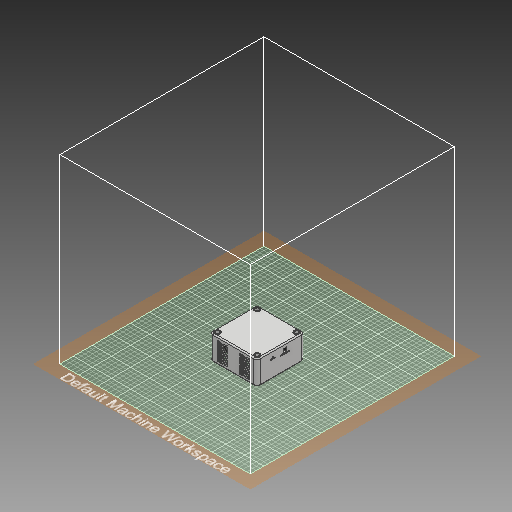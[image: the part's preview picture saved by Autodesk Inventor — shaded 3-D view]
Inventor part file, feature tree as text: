
AUTODESK INVENTOR PART (.ipt)
format: ipt  version: 2019 (Build 230136000, 136)  size: 2,817,024 bytes
history: native  units: mm
features: sketch x17, extrude x15, projected_geometry x15, other x5, fillet x4, reference x2, hole x1
ambient origin geometry x8: Origin, YZ Plane, XZ Plane, XY Plane, X Axis, Y Axis, Z Axis, Center Point
bodies: Body1 (feature_tree)
feature tree (59):
  other  "Твердое тело1"
  extrude  "Выдавливание1"  Depth=0.1mm
  extrude  "Выдавливание2"  Depth=0.3mm
  extrude  "Выдавливание3"  Depth=0.3mm
  fillet  "Сопряжение1"  Radius=0.3mm
  extrude  "Выдавливание5"  Depth=0.3mm
  extrude  "Выдавливание6"  Depth=2.1mm TaperAngle=0.0deg
  extrude  "Выдавливание7"  Depth=49.0mm TaperAngle=0.0deg
  extrude  "Выдавливание8"  Depth=2.5mm TaperAngle=0.0deg
  fillet  "Сопряжение2"  Radius=2.5mm
  fillet  "Сопряжение3"  Radius=12.0mm
  fillet  "Сопряжение4"  Radius=12.0mm
  extrude  "Выдавливание9"  Depth=12.0mm
  extrude  "Выдавливание10"  Depth=12.0mm
  extrude  "Выдавливание12"  Depth=1.4mm
  hole  "Отверстие1"  [1 undecoded]
  extrude  "Выдавливание13"  Depth=1.4mm
  extrude  "Выдавливание14"  Depth=1.4mm
  other  "Рельеф1"
  extrude  "Выдавливание15"  Depth=7.0mm
  extrude  "Выдавливание16"  Depth=7.0mm
  extrude  "Выдавливание17"  Depth=7.0mm
  sketch  "Эскиз1"
  reference  "Ссылка1"
  sketch  "Эскиз2"
  reference  "Ссылка2"
  projected_geometry  "Спроецированная петля1"
  sketch  "Эскиз3"
  projected_geometry  "Спроецированная петля2"
  sketch  "Эскиз4"
  sketch  "Эскиз5"
  sketch  "Эскиз6"
  sketch  "Эскиз7"
  sketch  "Эскиз8"
  sketch  "Эскиз9"
  sketch  "Эскиз10"
  projected_geometry  "Спроецированная петля3"
  sketch  "Эскиз11"
  sketch  "Эскиз13"
  sketch  "Эскиз15"
  sketch  "Эскиз16"
  projected_geometry  "Спроецированная петля5"
  projected_geometry  "Спроецированная петля6"
  projected_geometry  "Спроецированная петля7"
  projected_geometry  "Спроецированная петля8"
  projected_geometry  "Спроецированная петля9"
  projected_geometry  "Спроецированная петля10"
  projected_geometry  "Спроецированная петля11"
  projected_geometry  "Спроецированная петля12"
  sketch  "Эскиз17"
  sketch  "Эскиз18"
  projected_geometry  "Спроецированная петля13"
  projected_geometry  "Спроецированная петля14"
  projected_geometry  "Спроецированная петля15"
  projected_geometry  "Спроецированная петля16"
  sketch  "Эскиз19"
  other  "<userpath>\Documents\GitHub\Tesla_coil_V1\3dModels\TeslaCoil.iam"
  other  "TeslaCoil.iam"
  other  "TopBox:1"
note: 1 required parameter value undecoded (feature->parameter linkage not recoverable at this tier; creation-order binding heuristic only, values carry confidence <= 0.55)
